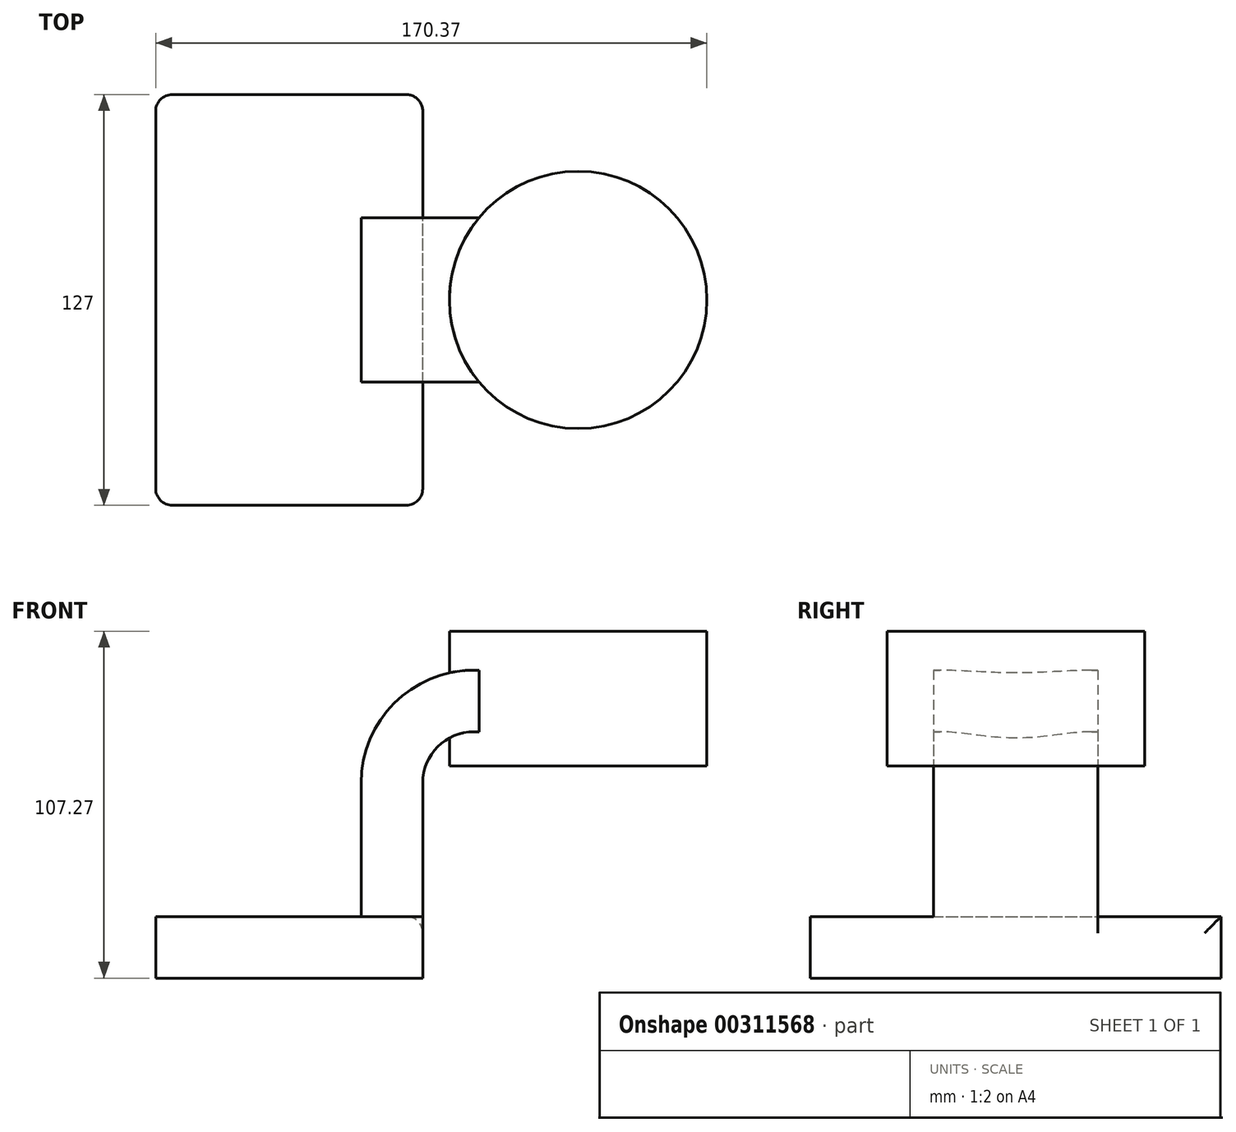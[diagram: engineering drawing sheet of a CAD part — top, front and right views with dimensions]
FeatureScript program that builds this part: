
annotation { "Feature Type Name" : "Feature", "Feature Type Description" : "" }
export const myFeature = defineFeature(function(context is Context, id is Id, definition is map)
    precondition{}
    {
        {
            var Q0;
            Q0=qCreatedBy(makeId("Front.planeOp"),FACE);
            var sketch = newSketch(context, id + "F0", { "sketchPlane" : qUnion([Q0])});
            skLineSegment(sketch, "E0.bottom", {"start": v(-41.28, -9.53) * mm, "end": v(41.28, -9.53) * mm});
            skLineSegment(sketch, "E0.top", {"start": v(-41.28, 9.52) * mm, "end": v(41.27, 9.52) * mm});
            skLineSegment(sketch, "E0.left", {"start": v(-41.27, -9.53) * mm, "end": v(-41.28, 9.52) * mm});
            skLineSegment(sketch, "E0.right", {"start": v(41.28, -9.53) * mm, "end": v(41.27, 9.52) * mm});
            skPoint(sketch, "E0.middle", {"position": v(0, 0) * mm});
            skLineSegment(sketch, "E1", {"start": v(41.27, 9.52) * mm, "end": v(41.27, 50.8) * mm});
            skArc(sketch, "E2", {"start": v(41.27, 50.8) * mm, "mid": v(45.92, 62.03) * mm, "end": v(57.15, 66.67) * mm});
            skLineSegment(sketch, "E3", {"start": v(57.15, 66.67) * mm, "end": v(89.3, 66.67) * mm});
            skLineSegment(sketch, "E4.bottom", {"start": v(75.84, 97.74) * mm, "end": v(129.1, 97.74) * mm});
            skLineSegment(sketch, "E4.top", {"start": v(75.84, 56.05) * mm, "end": v(129.1, 56.05) * mm});
            skLineSegment(sketch, "E4.left", {"start": v(75.84, 97.74) * mm, "end": v(75.84, 56.05) * mm});
            skLineSegment(sketch, "E4.right", {"start": v(129.1, 97.74) * mm, "end": v(129.1, 56.05) * mm});
            skLineSegment(sketch, "E5.0", {"start": v(57.15, 85.72) * mm, "end": v(89.3, 85.72) * mm});
            skArc(sketch, "E5.1", {"start": v(22.22, 50.8) * mm, "mid": v(32.45, 75.5) * mm, "end": v(57.15, 85.72) * mm});
            skLineSegment(sketch, "E5.2", {"start": v(22.22, 9.52) * mm, "end": v(22.22, 50.8) * mm});
            skLineSegment(sketch, "E6", {"start": v(89.3, 56.05) * mm, "end": v(89.3, 97.74) * mm});
            skFitSpline(sketch, "E7", {"points": [v(-41.28, 9.52) * mm, v(75.84, 85.72) * mm], "startDerivative": vector(12.17, 171.92) * mm, "endDerivative": vector(227.52, -12.05) * mm});
            skSolve(sketch);
        }
        {
            var Q0;
            Q0=makeQuery(id+"F0.imprint","IMPRINT",FACE,{"disambiguationData":[TD([[makeQuery(id+"F0.imprint","IMPRINT",EDGE,{"derivedFrom":sQuery(id+"F0.wireOp",EDGE,"E0.bottom")}),1.0]])]});
            extrude(context, id + "F1", {"entities" : qUnion([Q0]), "endBound" : BoundingType.SYMMETRIC, "depth" : 127 * mm});
        }
        {
            var Q0;
            {var subQ5=sQuery(id+"F0.wireOp",EDGE,"E1");Q0=makeQuery(id+"F0.imprint","IMPRINT",FACE,{"disambiguationData":[TD([[makeQuery(id+"F0.imprint","IMPRINT",EDGE,{"derivedFrom":subQ5}),1.0]])]});}
            var Q1;
            {var subQ0=sQuery(id+"F0.wireOp",EDGE,"E6");var subQ1=sQuery(id+"F0.wireOp",EDGE,"E3");var subQ2=makeQuery(id+"F0.imprint","INTERSECT",VERTEX,{"derivedFrom":[subQ1,subQ0]});Q1=makeQuery(id+"F0.imprint","IMPRINT",FACE,{"disambiguationData":[TD([[makeQuery(id+"F0.imprint","IMPRINT",EDGE,{"disambiguationData":[TD([[subQ2,1.0]])],"derivedFrom":subQ1}),1.0]])]});}
            extrude(context, id + "F2", {"entities" : qUnion([Q0, Q1]), "operationType" : NewBodyOperationType.ADD, "endBound" : BoundingType.SYMMETRIC, "depth" : 50.8 * mm});
        }
        {
            var Q0;
            {var subQ1=sQuery(id+"F0.wireOp",EDGE,"E5.1");Q0=makeQuery(id+"F0.imprint","IMPRINT",FACE,{"disambiguationData":[TD([[makeQuery(id+"F0.imprint","IMPRINT",EDGE,{"derivedFrom":subQ1}),1.0]])]});}
            extrude(context, id + "F3", {"entities" : qUnion([Q0]), "operationType" : NewBodyOperationType.ADD, "endBound" : BoundingType.SYMMETRIC, "depth" : 16.5 * mm});
        }
        {
            var Q0;
            {var subQ4=sQuery(id+"F0.wireOp",EDGE,"E4.right");Q0=makeQuery(id+"F0.imprint","IMPRINT",FACE,{"disambiguationData":[TD([[makeQuery(id+"F0.imprint","IMPRINT",EDGE,{"derivedFrom":subQ4}),-1.0]])]});}
            var Q1;
            Q1=sQuery(id+"F0.wireOp",EDGE,"E6");
            revolve(context, id + "F4", {"operationType" : NewBodyOperationType.ADD, "entities" : qUnion([Q0]), "axis" : qUnion([Q1]), "revolveType" : RevolveType.FULL});
        }
        {
            var Q0;
            {var subQ0=sQuery(id+"F0.wireOp",EDGE,"E1");var subQ1=sQuery(id+"F0.wireOp",EDGE,"E0.top");var subQ2=sQuery(id+"F0.wireOp",EDGE,"E0.right");Q0=makeQuery(id+"F2.boolean.opBoolean","SPLIT",EDGE,{"disambiguationData":[TD([makeQuery(id+"F1.opExtrude","CAP_FACE",FACE,{"disambiguationData":[OSD([sQuery(id+"F0.wireOp",EDGE,"E0.bottom"),subQ1,sQuery(id+"F0.wireOp",EDGE,"E0.left"),subQ2])],"isStart":true})])],"derivedFrom":makeQuery(id+"F1.opExtrude","SWEPT_EDGE",EDGE,{"disambiguationData":[OSD([subQ1,subQ2,subQ0])]})});}
            var Q1;
            Q1=makeQuery(id+"F1.opExtrude","CAP_EDGE",EDGE,{"disambiguationData":[OSD([sQuery(id+"F0.wireOp",EDGE,"E0.left")])],"isStart":true});
            var Q2;
            Q2=makeQuery(id+"F1.opExtrude","CAP_EDGE",EDGE,{"disambiguationData":[OSD([sQuery(id+"F0.wireOp",EDGE,"E0.left")])],"isStart":false});
            var Q3;
            Q3=makeQuery(id+"F1.opExtrude","CAP_EDGE",EDGE,{"disambiguationData":[OSD([sQuery(id+"F0.wireOp",EDGE,"E0.right")])],"isStart":true});
            var Q4;
            Q4=makeQuery(id+"F1.opExtrude","CAP_EDGE",EDGE,{"disambiguationData":[OSD([sQuery(id+"F0.wireOp",EDGE,"E0.right")])],"isStart":false});
            fillet(context, id + "F5", {"entities" : qUnion([Q0, Q1, Q2, Q3, Q4]), "radius" : 5.08 * mm, "tangentPropagation" : true, "allowEdgeOverflow" : false});
        }
    });
